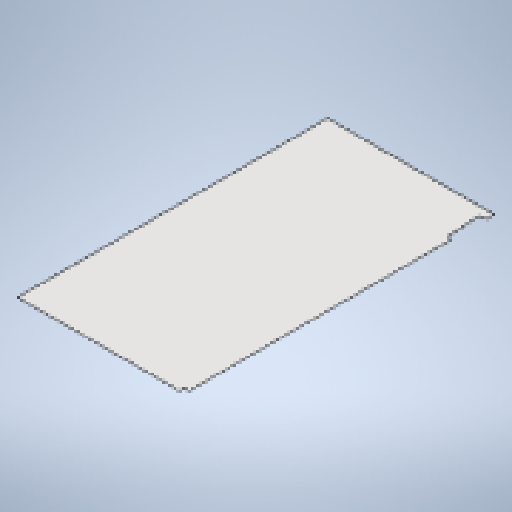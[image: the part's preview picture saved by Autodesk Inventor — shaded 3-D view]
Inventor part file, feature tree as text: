
AUTODESK INVENTOR PART (.ipt)
format: ipt  version: 2025.1 (Build 291241020, 241B)  size: 210,432 bytes
history: native  units: mm
features: other x2, sheet_metal_op x1, chamfer x1, sketch x1
ambient origin geometry x8: Origin, YZ Plane, XZ Plane, XY Plane, X Axis, Y Axis, Z Axis, Center Point
bodies: Body1 (feature_tree)
feature tree (5):
  sheet_metal_op  "Face3"
  chamfer  "Corner Round1"
  sketch  "Sketch1"  dims[d61=500.0mm d154=1385.0mm d155=2575.0mm d156=2.0mm d157=40.0mm d158=15.0mm d159=290.0mm d161=40.0mm d162=2220.0mm d163=10.0mm d164=150.0mm d165=5.0mm d166=590.0mm d167=590.0mm d168=675.0mm d169=520.0mm]
  other  "Plate5"
  other  "Definition1"
